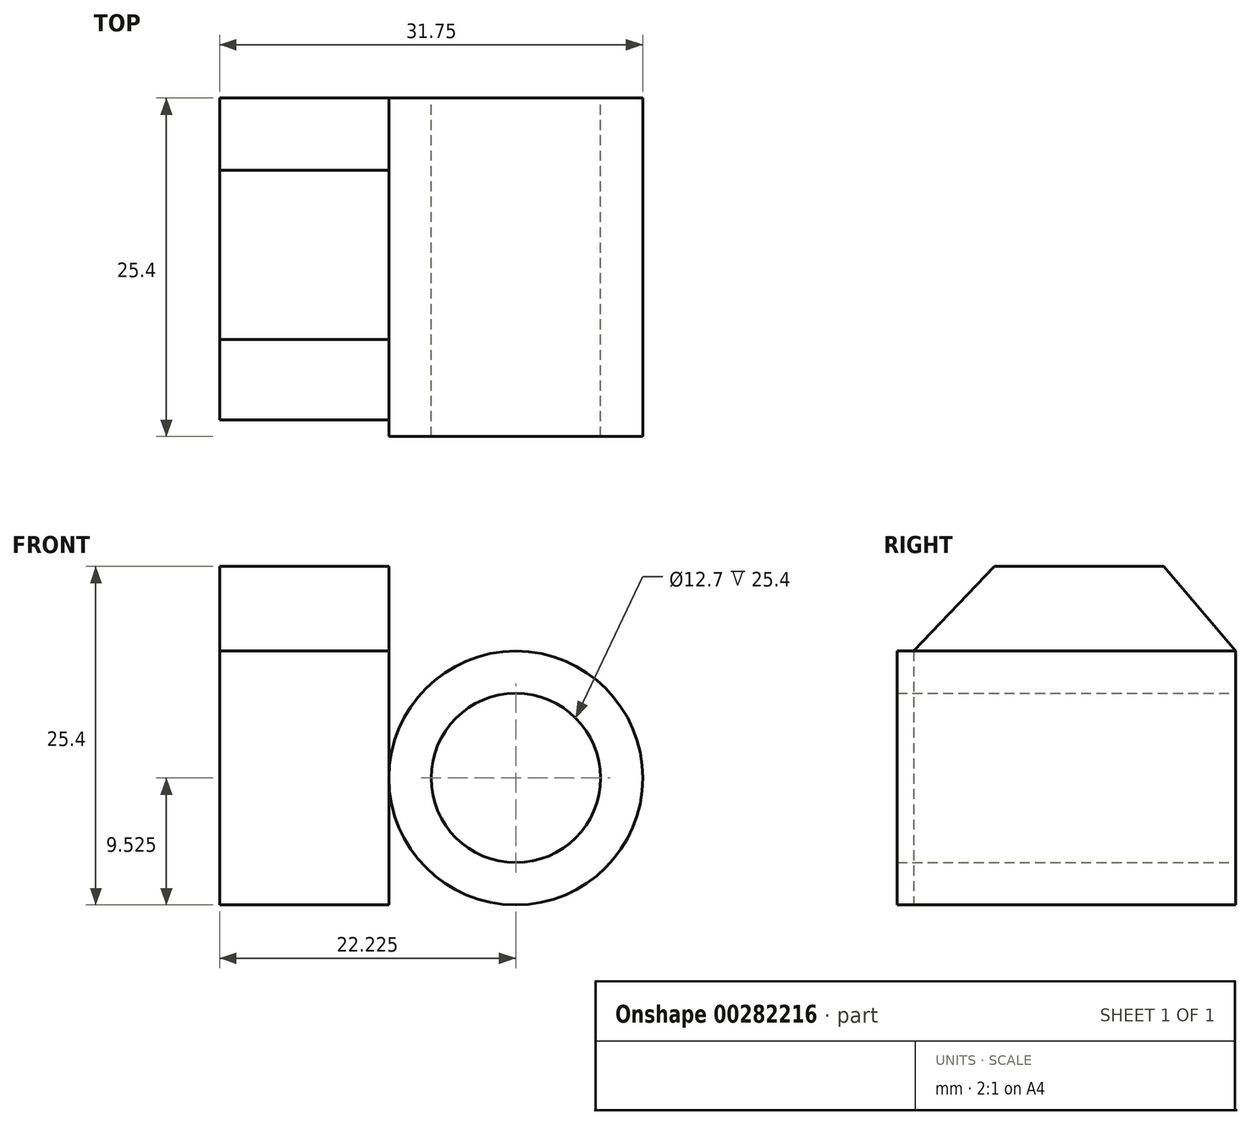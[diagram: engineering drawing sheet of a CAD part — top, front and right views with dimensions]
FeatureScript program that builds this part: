
annotation { "Feature Type Name" : "Feature", "Feature Type Description" : "" }
export const myFeature = defineFeature(function(context is Context, id is Id, definition is map)
    precondition{}
    {
        {
            var Q0;
            Q0=qCreatedBy(makeId("Right.planeOp"),FACE);
            var sketch = newSketch(context, id + "F0", { "sketchPlane" : qUnion([Q0])});
            skLineSegment(sketch, "E0", {"start": v(0, 0) * mm, "end": v(0, 19.05) * mm});
            skLineSegment(sketch, "E1", {"start": v(0, 19.05) * mm, "end": v(-5.41, 25.4) * mm});
            skLineSegment(sketch, "E2", {"start": v(-5.41, 25.4) * mm, "end": v(-18.11, 25.4) * mm});
            skLineSegment(sketch, "E3", {"start": v(-18.11, 25.4) * mm, "end": v(-24.15, 19.05) * mm});
            skLineSegment(sketch, "E4", {"start": v(-24.15, 19.05) * mm, "end": v(-24.15, 0) * mm});
            skLineSegment(sketch, "E5", {"start": v(-24.15, 0) * mm, "end": v(0, 0) * mm});
            skSolve(sketch);
        }
        {
            var Q0;
            Q0 = qSketchRegion(id + "F0", true);
            extrude(context, id + "F1", {"entities" : qUnion([Q0]), "depth" : 12.7 * mm});
        }
        {
            var Q0;
            Q0=qCreatedBy(makeId("Front.planeOp"),FACE);
            var sketch = newSketch(context, id + "F2", { "sketchPlane" : qUnion([Q0])});
            skCircle(sketch, "E6", {"center": v(22.23, 9.53) * mm, "radius": 9.52 * mm});
            skCircle(sketch, "E7", {"center": v(22.23, 9.53) * mm, "radius": 6.35 * mm});
            skSolve(sketch);
        }
        {
            var Q0;
            Q0 = qSketchRegion(id + "F2", true);
            extrude(context, id + "F3", {"entities" : qUnion([Q0]), "operationType" : NewBodyOperationType.ADD, "depth" : 25.4 * mm});
        }
    });
